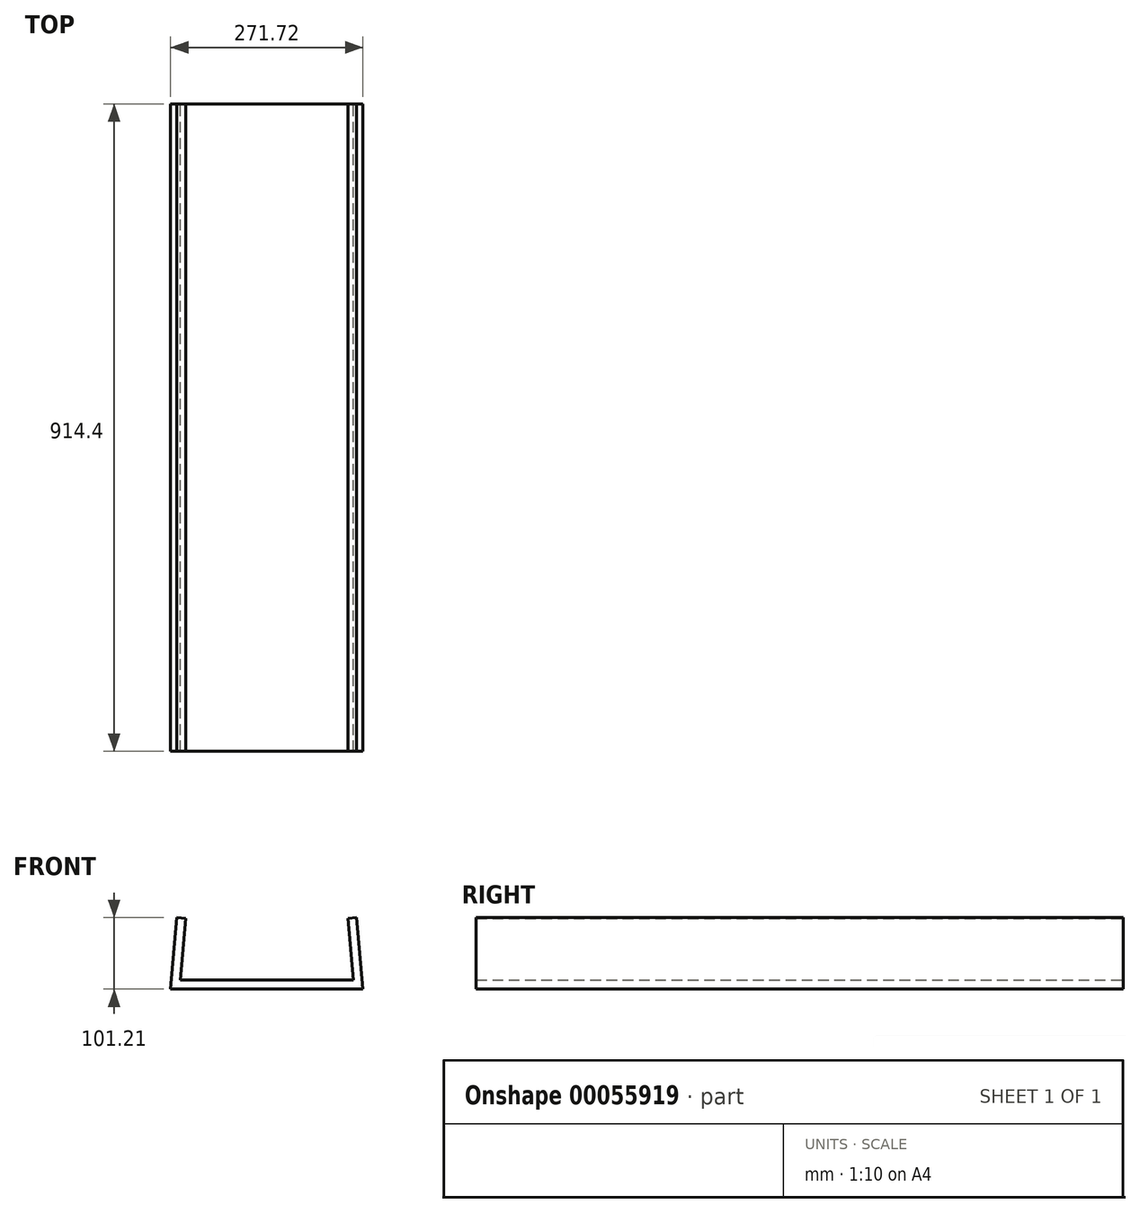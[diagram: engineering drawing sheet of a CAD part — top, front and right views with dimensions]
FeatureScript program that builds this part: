
annotation { "Feature Type Name" : "Feature", "Feature Type Description" : "" }
export const myFeature = defineFeature(function(context is Context, id is Id, definition is map)
    precondition{}
    {
        {
            var Q0;
            Q0=qCreatedBy(makeId("Front.planeOp"),FACE);
            var sketch = newSketch(context, id + "F0", { "sketchPlane" : qUnion([Q0])});
            skCircle(sketch, "E0", {"center": v(0, 0) * mm, "radius": 127 * mm});
            skLineSegment(sketch, "E1", {"start": v(-127, 0) * mm, "end": v(-135.86, -101.21) * mm});
            skLineSegment(sketch, "E2", {"start": v(-127, 0) * mm, "end": v(-127, -76.64) * mm});
            skLineSegment(sketch, "E3", {"start": v(0, 0) * mm, "end": v(0, -56.27) * mm});
            skLineSegment(sketch, "E4", {"start": v(-135.86, -101.21) * mm, "end": v(0, -101.21) * mm});
            skLineSegment(sketch, "E5", {"start": v(-127, 0) * mm, "end": v(-114.35, -1.1) * mm});
            skLineSegment(sketch, "E6", {"start": v(-114.35, -1.1) * mm, "end": v(-122, -88.51) * mm});
            skLineSegment(sketch, "E7", {"start": v(0, -88.51) * mm, "end": v(-122, -88.51) * mm});
            skLineSegment(sketch, "E8.MirrorCS", {"start": v(127, 0) * mm, "end": v(114.35, -1.1) * mm});
            skLineSegment(sketch, "E9.MirrorCS", {"start": v(127, 0) * mm, "end": v(135.86, -101.21) * mm});
            skLineSegment(sketch, "E10.MirrorCS", {"start": v(114.35, -1.1) * mm, "end": v(122, -88.51) * mm});
            skLineSegment(sketch, "E11.MirrorCS", {"start": v(135.86, -101.21) * mm, "end": v(0, -101.21) * mm});
            skLineSegment(sketch, "E12.MirrorCS", {"start": v(0, -88.51) * mm, "end": v(122, -88.51) * mm});
            skSolve(sketch);
        }
        {
            var Q0;
            {var subQ0=sQuery(id+"F0.wireOp",EDGE,"E5");Q0=makeQuery(id+"F0.imprint","IMPRINT",FACE,{"disambiguationData":[TD([[makeQuery(id+"F0.imprint","IMPRINT",EDGE,{"derivedFrom":subQ0}),-1.0]])]});}
            var Q1;
            {var subQ1=sQuery(id+"F0.wireOp",EDGE,"E1");Q1=makeQuery(id+"F0.imprint","IMPRINT",FACE,{"disambiguationData":[TD([[makeQuery(id+"F0.imprint","IMPRINT",EDGE,{"derivedFrom":subQ1}),1.0]])]});}
            var Q2;
            {var subQ3=sQuery(id+"F0.wireOp",EDGE,"E0");var subQ6=sQuery(id+"F0.wireOp",EDGE,"E4");var subQ8=makeQuery(id+"F0.imprint","INTERSECT",VERTEX,{"derivedFrom":[subQ3,subQ6]});Q2=makeQuery(id+"F0.imprint","IMPRINT",FACE,{"disambiguationData":[TD([[makeQuery(id+"F0.imprint","IMPRINT",EDGE,{"disambiguationData":[TD([[subQ8,1.0]])],"derivedFrom":subQ3}),1.0]])]});}
            var Q3;
            {var subQ0=sQuery(id+"F0.wireOp",EDGE,"E9.MirrorCS");Q3=makeQuery(id+"F0.imprint","IMPRINT",FACE,{"disambiguationData":[TD([[makeQuery(id+"F0.imprint","IMPRINT",EDGE,{"derivedFrom":subQ0}),-1.0]])]});}
            var Q4;
            {var subQ0=sQuery(id+"F0.wireOp",EDGE,"E8.MirrorCS");Q4=makeQuery(id+"F0.imprint","IMPRINT",FACE,{"disambiguationData":[TD([[makeQuery(id+"F0.imprint","IMPRINT",EDGE,{"derivedFrom":subQ0}),1.0]])]});}
            extrude(context, id + "F1", {"entities" : qUnion([Q0, Q1, Q2, Q3, Q4]), "depth" : 914.4 * mm});
        }
    });
